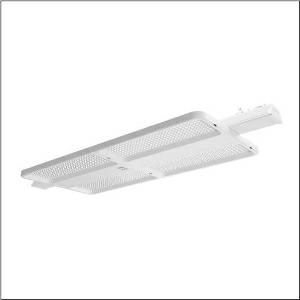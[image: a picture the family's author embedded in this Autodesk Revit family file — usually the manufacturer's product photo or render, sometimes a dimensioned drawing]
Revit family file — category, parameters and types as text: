
# Revit family: highbay_21_fur_licross_r__tragschiene_maxi_52hn11db4mla03_be93
name_source: partatom
category: Lighting Fixtures
units: mm (PartAtom-declared; Revit-internal decimal feet)

## family parameters
Cut with Voids When Loaded = No
Host = Face
Light Source = No
Part Type = Normal
Room Calculation Point = No
Round Connector Dimension = Use Diameter
Shared = No

## types (1)
- --- (1 x LED, 28000 lm, 144 W, 4000K)
    Apparent Load = 144 VA
    CIE Flux Codes = 89 97 99 100 100
    Color Rendering = 80
    Color Temperature = 4000K
    Default Elevation = 1800 mm
    Description = high bay luminaire Highbay 21 for Licross® trunking rail maxi; direct symmetric narrow distribution, light control with lens of PMMA; UGR ≤ 19 (X = 4H | Y = 8H | S = 0.25H | reflection values 70/50/20); luminous flux: 28.000lm; light colour: 840, colour temperature: 4000K, MacAdam ≤ 3 SDCM (initial), colour rendering: CRI > 80; luminous efficacy: 194,4lm/W; rated service life: 75.000h (L80/B50) at AT= ta max; control: DALI 2; for wired networking: open and standardized DALI2 interface enables full flexibility and future-proofing for changes in use or functional adaptation through individual programming; multi-sensor luminaire consisting of a DALI2 multi-sensor and DALI2 ECG; multi-sensor luminaire for wired connection to a DALI2 application controller (e.g., SITECO Connect 11 or 21); can also be connected to existing on-site lighting or building automation systems upon request; integrated DALI2 sensor certified according to IEC 62386, Parts 101, 103, 303, and 304; integrated DALI2 ECG provides luminaire data (according to IEC 62386, Part 251), energy data (Part 252), and monitoring and analytics data (Part 253) to higher-level systems for further processing; luminaire with PIR sensor (passive-infrared); with light sensor; luminaire connection: plug, 5-pole, with phase selectionmains connection: 230..240V, AC 50/60Hz; connected load: 144W; protection rating (complete): IP64; insulation class (complete): insulation class I (protective earthing); protection symbol: D; certification: CE, ENEC, VDE, UKCA; internal wiring halogen-free; luminaire corresponds to IFS (International Featured Standards) requirements for safety and quality in the food industry; LABS conformity tested according to VDMA 24364:2018-05; housing frame of high-performance plastic PA6, matt traffic white (RAL 9016); cover of PMMA; fixing on rail side of steel, galvanised, white; blank cover of PC/ABS, traffic white (RAL 9016); dimension (LxWxH): 1.250 x 442 x 71mm; permissible operating ambient temperature: -20..+45°C (reducing of maximum allowable ambient temperature of 5°C with ceiling mounting); packaging unit: 1 piece
    Height = 72 mm  [stored 0.23622 ft]
    Lamp = 1 x LED
    Lamp Light Flux = 28000 lm
    Lamp Power = 144 W
    Lamp count = 1
    Length = 946 mm
    Luminous efficacy = 194 lm/W
    Manufacturer = Siteco
    ModVariant = No
    Model = 52HN11DB4MLA03
    Mounting Place = Ceiling
    Mounting Type = Pendant
    Number of Poles = 1
    OnlyDefault = Yes
    Power Factor = 1
    Product Name = Highbay 21 für Licross® Tragschiene maxi
    Product group = high bay luminaire
    ProductGroupID = 901
    Protection Class = Protection class I
    Protection Degree = IP 64
    RLX_Detail_Level = 1
    RLX_Emergency_Light_Flux = 0 lm
    RLX_Emergency_Type = 0
    RLX_Emergency_Type_DB = No
    RlxData = <blob elided: 131449 chars, md5=bcef44a1>
    Socket = socket
    Standby Power = 0 W
    System Light Flux = 27999 lm
    System Power = 144 W
    Type Comments = factory setting: luminous flux: 100 % | dim-lin: 254 | 668 mA
    Type Image = l_1363271.jpg
    URL = http://relux.com
    VarID = @adj_009309
    Voltage = 0 V
    Weight = 0.00 kg
    Width = 442 mm

note: [stored X ft] marks values corroborated as IEEE doubles in the binary element streams (Revit-internal decimal feet)

## geometry (parser evidence)
native form markers: Blend x4, Sweep x9
no freeform markers — native parametric forms only
